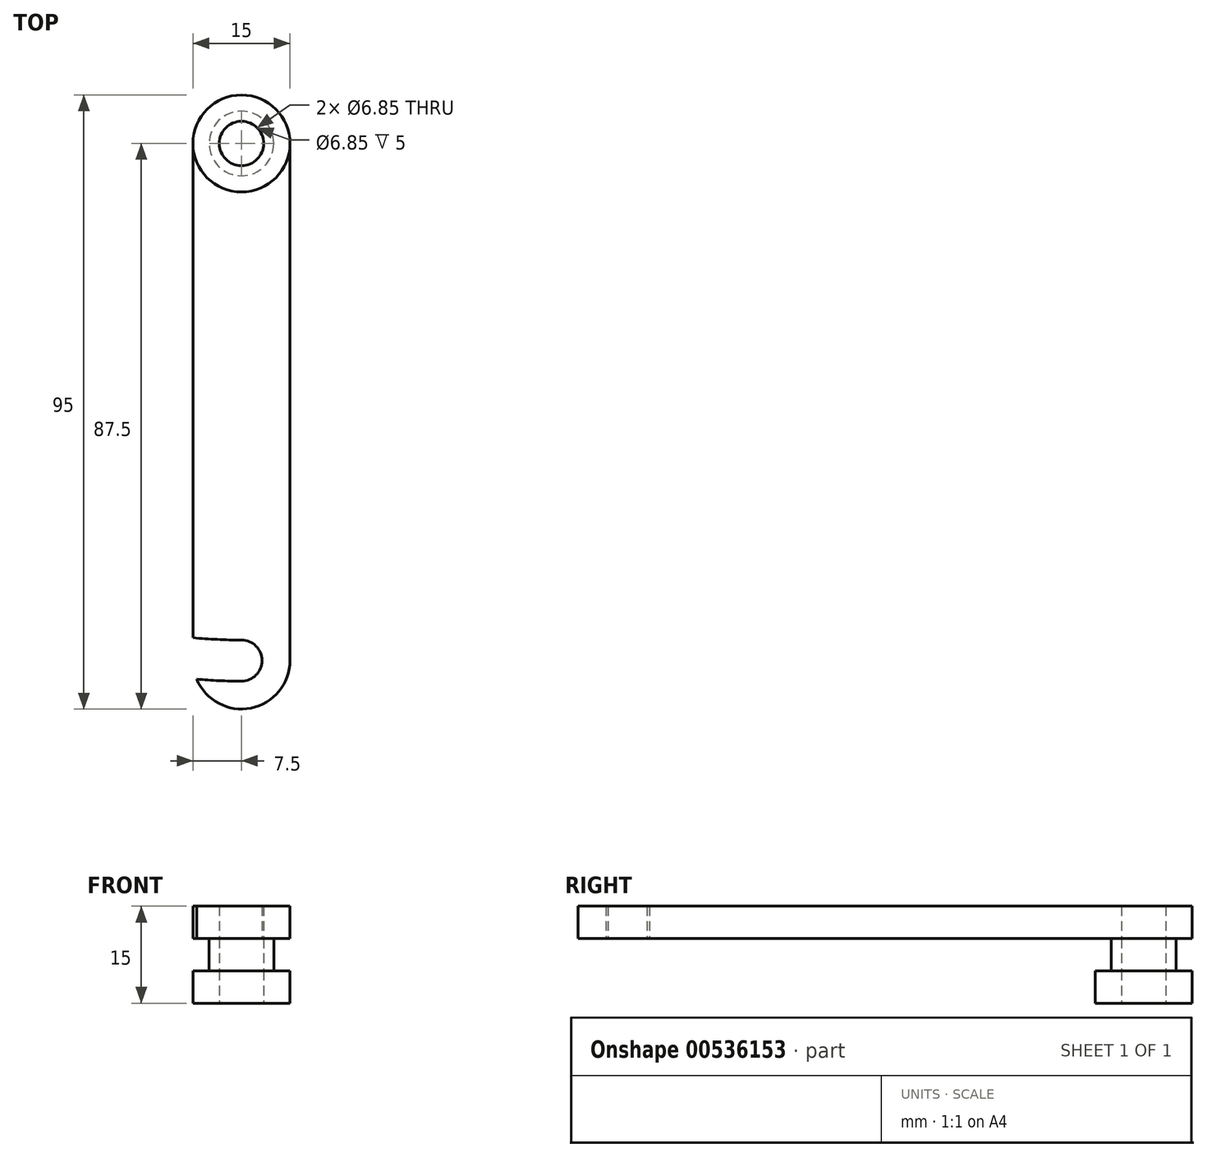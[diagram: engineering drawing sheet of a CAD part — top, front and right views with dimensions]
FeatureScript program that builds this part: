
annotation { "Feature Type Name" : "Feature", "Feature Type Description" : "" }
export const myFeature = defineFeature(function(context is Context, id is Id, definition is map)
    precondition{}
    {
        {
            var Q0;
            Q0=qCreatedBy(makeId("Top.planeOp"),FACE);
            var sketch = newSketch(context, id + "F0", { "sketchPlane" : qUnion([Q0])});
            skCircle(sketch, "E0", {"center": v(0, 0) * mm, "radius": 7.5 * mm});
            skCircle(sketch, "E1", {"center": v(0, 0) * mm, "radius": 3.43 * mm});
            skSolve(sketch);
        }
        {
            var Q0;
            Q0 = qSketchRegion(id + "F0", true);
            extrude(context, id + "F1", {"entities" : qUnion([Q0]), "depth" : 5 * mm, "offsetDistance" : 25 * mm});
        }
        {
            var Q0;
            Q0=makeQuery(id+"F1.opExtrude","CAP_FACE",FACE,{"disambiguationData":[OSD([sQuery(id+"F0.wireOp",EDGE,"E0"),sQuery(id+"F0.wireOp",EDGE,"E1")])],"isStart":false});
            cPlane(context, id + "F2", {"entities" : qUnion([Q0]), "cplaneType" : CPlaneType.OFFSET, "offset" : 0 * mm, "width" : 150 * mm, "height" : 150 * mm});
        }
        {
            var Q0;
            Q0=qCreatedBy(id+"F2.planeOp",FACE);
            var sketch = newSketch(context, id + "F3", { "sketchPlane" : qUnion([Q0])});
            skCircle(sketch, "E2.0", {"center": v(0, 0) * mm, "radius": 3.43 * mm});
            skCircle(sketch, "E3", {"center": v(0, 0) * mm, "radius": 5 * mm});
            skSolve(sketch);
        }
        {
            var Q0;
            Q0 = qSketchRegion(id + "F3", true);
            extrude(context, id + "F4", {"entities" : qUnion([Q0]), "depth" : 5 * mm, "offsetDistance" : 25 * mm});
        }
        {
            var Q0;
            Q0=makeQuery(id+"F4.opExtrude","CAP_FACE",FACE,{"disambiguationData":[OSD([sQuery(id+"F3.wireOp",EDGE,"E2.0"),sQuery(id+"F3.wireOp",EDGE,"E3")])],"isStart":false});
            cPlane(context, id + "F5", {"entities" : qUnion([Q0]), "cplaneType" : CPlaneType.OFFSET, "offset" : 0 * mm, "width" : 150 * mm, "height" : 150 * mm});
        }
        {
            var Q0;
            Q0=qCreatedBy(id+"F5.planeOp",FACE);
            var sketch = newSketch(context, id + "F6", { "sketchPlane" : qUnion([Q0])});
            skCircle(sketch, "E4.0", {"center": v(0, 0) * mm, "radius": 3.43 * mm});
            skArc(sketch, "E5.0.0", {"start": v(7.5, 0) * mm, "mid": v(0, 7.5) * mm, "end": v(-7.5, 0) * mm});
            skLineSegment(sketch, "E6", {"start": v(-7.5, 0) * mm, "end": v(-7.5, -76.46) * mm});
            skLineSegment(sketch, "E7", {"start": v(7.5, 0) * mm, "end": v(7.5, -80) * mm});
            skArc(sketch, "E8", {"start": v(-6.92, -82.89) * mm, "mid": v(1.47, -87.35) * mm, "end": v(7.5, -80) * mm});
            skArc(sketch, "E9", {"start": v(0, -83.17) * mm, "mid": v(3.17, -80) * mm, "end": v(0, -76.83) * mm});
            skArc(sketch, "E10", {"start": v(-7.5, -76.46) * mm, "mid": v(-3.75, -76.73) * mm, "end": v(0, -76.83) * mm});
            skArc(sketch, "E11", {"start": v(-6.92, -82.89) * mm, "mid": v(-3.46, -83.1) * mm, "end": v(0, -83.17) * mm});
            skLineSegment(sketch, "E12", {"start": v(0, -76.83) * mm, "end": v(0, -83.17) * mm, "construction": true});
            skPoint(sketch, "E13.orphan", {"position": v(-7.5, -80) * mm});
            skSolve(sketch);
        }
        {
            var Q0;
            Q0 = qSketchRegion(id + "F6", true);
            extrude(context, id + "F7", {"entities" : qUnion([Q0]), "depth" : 5 * mm, "offsetDistance" : 25 * mm});
        }
    });
